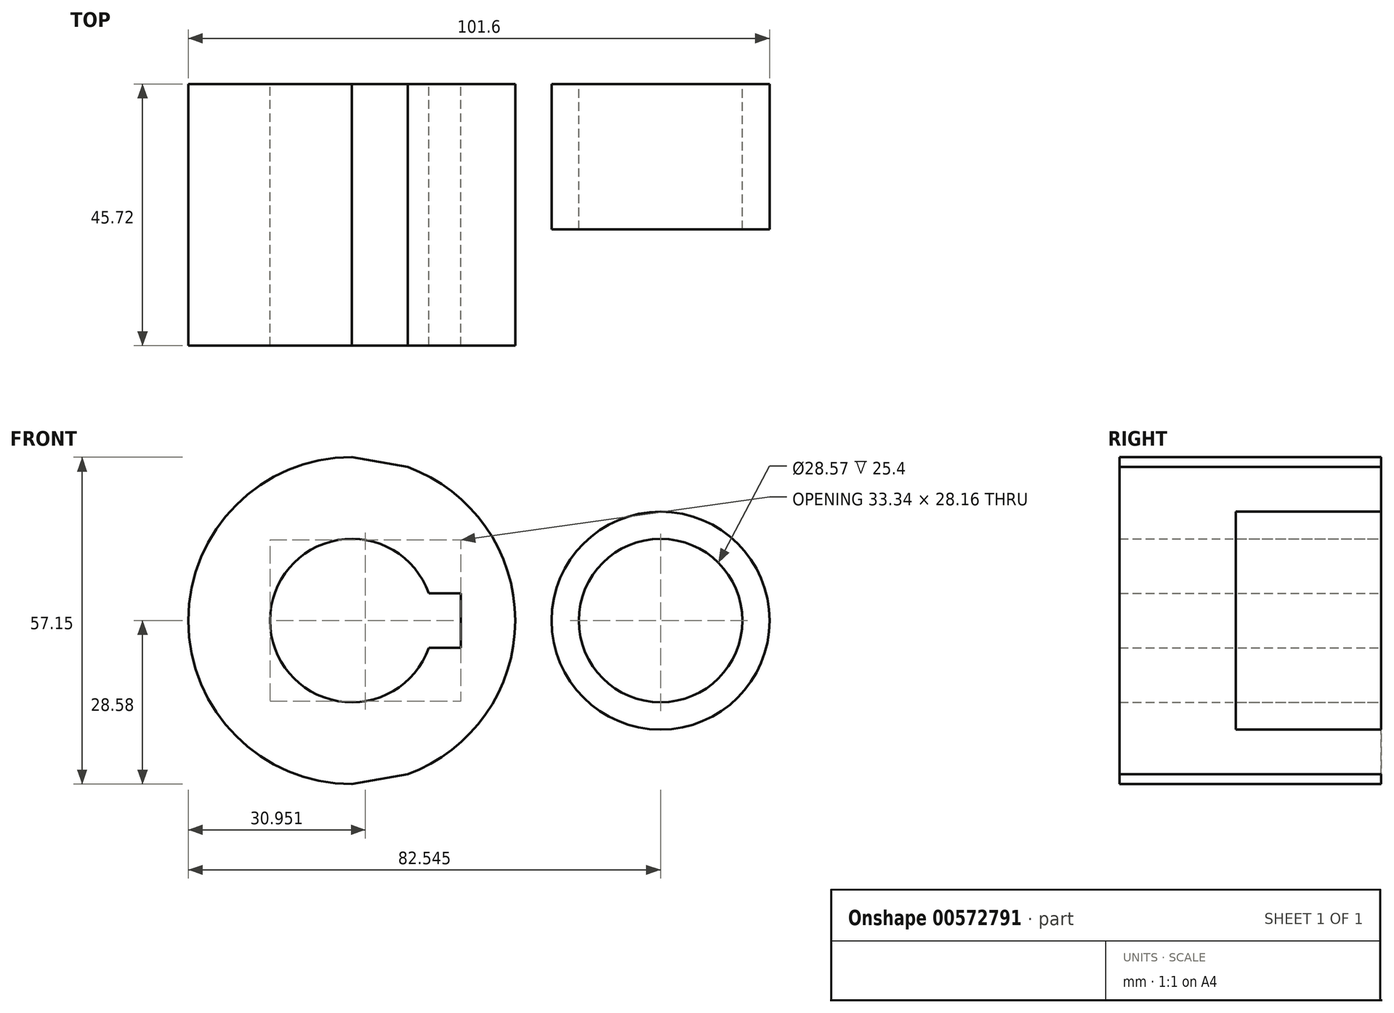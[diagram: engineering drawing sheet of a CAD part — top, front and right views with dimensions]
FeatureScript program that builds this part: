
annotation { "Feature Type Name" : "Feature", "Feature Type Description" : "" }
export const myFeature = defineFeature(function(context is Context, id is Id, definition is map)
    precondition{}
    {
        {
            var Q0;
            Q0=qCreatedBy(makeId("Front.planeOp"),FACE);
            var sketch = newSketch(context, id + "F0", { "sketchPlane" : qUnion([Q0])});
            skCircle(sketch, "E0", {"center": v(0, 0) * mm, "radius": 28.57 * mm});
            skCircle(sketch, "E1", {"center": v(53.98, 0) * mm, "radius": 19.05 * mm});
            skLineSegment(sketch, "E2", {"start": v(0, 28.58) * mm, "end": v(53.98, 19.05) * mm});
            skLineSegment(sketch, "E3", {"start": v(0, -28.58) * mm, "end": v(53.98, -19.05) * mm});
            skCircle(sketch, "E4", {"center": v(0, 0) * mm, "radius": 14.29 * mm});
            skCircle(sketch, "E5", {"center": v(53.98, 0) * mm, "radius": 14.29 * mm});
            skLineSegment(sketch, "E6.bottom", {"start": v(-19.05, 4.76) * mm, "end": v(19.05, 4.76) * mm});
            skLineSegment(sketch, "E6.top", {"start": v(-19.05, -4.76) * mm, "end": v(19.05, -4.76) * mm});
            skLineSegment(sketch, "E6.left", {"start": v(-19.05, 4.76) * mm, "end": v(-19.05, -4.76) * mm});
            skLineSegment(sketch, "E6.right", {"start": v(19.05, 4.76) * mm, "end": v(19.05, -4.76) * mm});
            skSolve(sketch);
        }
        {
            var Q0;
            {var subQ4=sQuery(id+"F0.wireOp",EDGE,"E6.left");Q0=makeQuery(id+"F0.imprint","IMPRINT",FACE,{"disambiguationData":[TD([[makeQuery(id+"F0.imprint","IMPRINT",EDGE,{"derivedFrom":subQ4}),-1.0]])]});}
            var Q1;
            {var subQ5=sQuery(id+"F0.wireOp",EDGE,"E6.left");Q1=makeQuery(id+"F0.imprint","IMPRINT",FACE,{"disambiguationData":[TD([[makeQuery(id+"F0.imprint","IMPRINT",EDGE,{"derivedFrom":subQ5}),1.0]])]});}
            var Q2;
            {var subQ0=sQuery(id+"F0.wireOp",EDGE,"E2");var subQ1=sQuery(id+"F0.wireOp",EDGE,"E0");var subQ2=makeQuery(id+"F0.imprint","INTERSECT",VERTEX,{"disambiguationData":[OD(1.0)],"derivedFrom":[subQ1,subQ0]});Q2=makeQuery(id+"F0.imprint","IMPRINT",FACE,{"disambiguationData":[TD([[makeQuery(id+"F0.imprint","IMPRINT",EDGE,{"disambiguationData":[TD([[subQ2,1.0]])],"derivedFrom":subQ1}),-1.0]])]});}
            var Q3;
            Q3=makeQuery(id+"F0.imprint","IMPRINT",FACE,{"disambiguationData":[TD([[makeQuery(id+"F0.imprint","IMPRINT",EDGE,{"derivedFrom":sQuery(id+"F0.wireOp",EDGE,"E5")}),-1.0]])]});
            extrude(context, id + "F1", {"entities" : qUnion([Q0, Q1, Q2, Q3]), "depth" : 25.4 * mm, "offsetDistance" : 25.4 * mm});
        }
        {
            var Q0;
            {var subQ4=sQuery(id+"F0.wireOp",EDGE,"E6.left");Q0=makeQuery(id+"F0.imprint","IMPRINT",FACE,{"disambiguationData":[TD([[makeQuery(id+"F0.imprint","IMPRINT",EDGE,{"derivedFrom":subQ4}),-1.0]])]});}
            var Q1;
            {var subQ5=sQuery(id+"F0.wireOp",EDGE,"E6.left");Q1=makeQuery(id+"F0.imprint","IMPRINT",FACE,{"disambiguationData":[TD([[makeQuery(id+"F0.imprint","IMPRINT",EDGE,{"derivedFrom":subQ5}),1.0]])]});}
            extrude(context, id + "F2", {"entities" : qUnion([Q0, Q1]), "operationType" : NewBodyOperationType.ADD, "depth" : 45.72 * mm, "offsetDistance" : 25.4 * mm});
        }
    });
